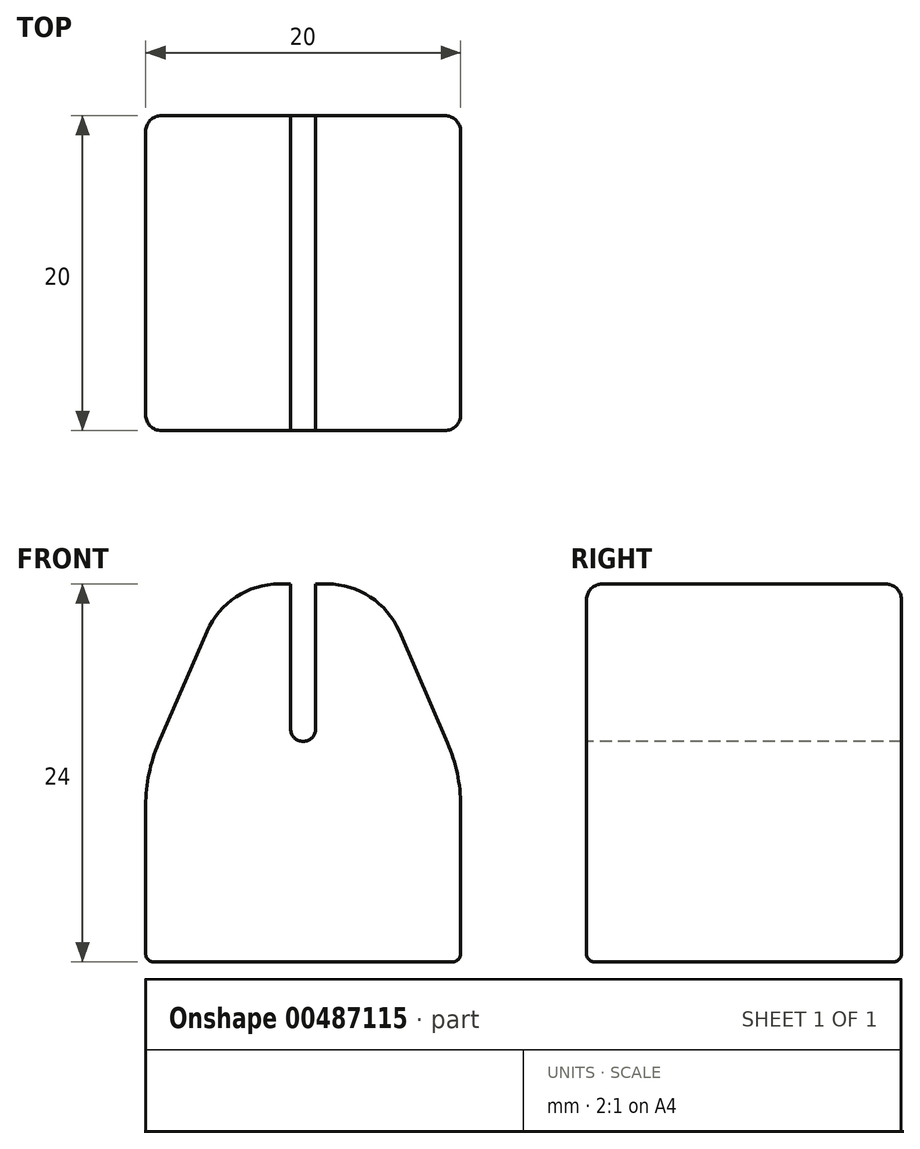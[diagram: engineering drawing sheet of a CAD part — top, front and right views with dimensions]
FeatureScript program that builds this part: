
annotation { "Feature Type Name" : "Feature", "Feature Type Description" : "" }
export const myFeature = defineFeature(function(context is Context, id is Id, definition is map)
    precondition{}
    {
        {
            var Q0;
            Q0=qCreatedBy(makeId("Front.planeOp"),FACE);
            var sketch = newSketch(context, id + "F0", { "sketchPlane" : qUnion([Q0])});
            skLineSegment(sketch, "E0.0.1", {"start": v(-4.8, 10) * mm, "end": v(-10, -2) * mm});
            skLineSegment(sketch, "E0.0.3", {"start": v(-0.8, 0) * mm, "end": v(-0.8, 10) * mm});
            skLineSegment(sketch, "E0.0.4", {"start": v(-0.8, 10) * mm, "end": v(-4.8, 10) * mm});
            skLineSegment(sketch, "E1.0.3", {"start": v(0.8, 10) * mm, "end": v(0.8, 0) * mm});
            skLineSegment(sketch, "E2", {"start": v(-10, -2) * mm, "end": v(-10, -14) * mm});
            skLineSegment(sketch, "E3", {"start": v(-10, -14) * mm, "end": v(10, -14) * mm});
            skLineSegment(sketch, "E4", {"start": v(0.8, 0) * mm, "end": v(-0.8, 0) * mm});
            skLineSegment(sketch, "E5", {"start": v(0, 0) * mm, "end": v(0, -14) * mm});
            skLineSegment(sketch, "E6.MirrorCS", {"start": v(10, -2) * mm, "end": v(10, -14) * mm});
            skLineSegment(sketch, "E7.MirrorCS", {"start": v(4.8, 10) * mm, "end": v(10, -2) * mm});
            skLineSegment(sketch, "E8.MirrorCS", {"start": v(0.8, 10) * mm, "end": v(4.8, 10) * mm});
            skLineSegment(sketch, "E9", {"start": v(-10, -2) * mm, "end": v(10, -2) * mm});
            skLineSegment(sketch, "E10", {"start": v(0, 0) * mm, "end": v(0, -2) * mm});
            skSolve(sketch);
        }
        {
            var Q0;
            Q0=makeQuery(id+"F0.imprint","IMPRINT",FACE,{"disambiguationData":[TD([[makeQuery(id+"F0.imprint","IMPRINT",EDGE,{"derivedFrom":sQuery(id+"F0.wireOp",EDGE,"E0.0.1")}),1.0]])]});
            var Q1;
            Q1=makeQuery(id+"F0.imprint","IMPRINT",FACE,{"disambiguationData":[TD([[makeQuery(id+"F0.imprint","IMPRINT",EDGE,{"derivedFrom":sQuery(id+"F0.wireOp",EDGE,"E1.0.2")}),1.0]])]});
            var Q2;
            {var subQ2=sQuery(id+"F0.wireOp",EDGE,"E1.0.3");Q2=makeQuery(id+"F0.imprint","IMPRINT",FACE,{"disambiguationData":[TD([[makeQuery(id+"F0.imprint","IMPRINT",EDGE,{"derivedFrom":subQ2}),1.0]])]});}
            var Q3;
            {var subQ0=sQuery(id+"F0.wireOp",EDGE,"E2");Q3=makeQuery(id+"F0.imprint","IMPRINT",FACE,{"disambiguationData":[TD([[makeQuery(id+"F0.imprint","IMPRINT",EDGE,{"derivedFrom":subQ0}),1.0]])]});}
            var Q4;
            {var subQ2=sQuery(id+"F0.wireOp",EDGE,"E5");Q4=makeQuery(id+"F0.imprint","IMPRINT",FACE,{"disambiguationData":[TD([[makeQuery(id+"F0.imprint","IMPRINT",EDGE,{"derivedFrom":subQ2}),1.0]])]});}
            extrude(context, id + "F1", {"entities" : qUnion([Q0, Q1, Q2, Q3, Q4]), "endBound" : BoundingType.SYMMETRIC, "depth" : 20 * mm, "offsetDistance" : 25 * mm});
        }
        {
            var Q0;
            Q0=makeQuery(id+"F1.opExtrude","SWEPT_EDGE",EDGE,{"disambiguationData":[OSD([sQuery(id+"F0.wireOp",EDGE,"E6.MirrorCS"),sQuery(id+"F0.wireOp",EDGE,"E7.MirrorCS")])]});
            var Q1;
            Q1=makeQuery(id+"F1.opExtrude","SWEPT_EDGE",EDGE,{"disambiguationData":[OSD([sQuery(id+"F0.wireOp",EDGE,"E0.0.1"),sQuery(id+"F0.wireOp",EDGE,"E2")])]});
            fillet(context, id + "F2", {"entities" : qUnion([Q0, Q1]), "radius" : 10 * mm, "tangentPropagation" : true, "allowEdgeOverflow" : false});
        }
        {
            var Q0;
            Q0=makeQuery(id+"F1.opExtrude","SWEPT_EDGE",EDGE,{"disambiguationData":[OSD([sQuery(id+"F0.wireOp",EDGE,"E7.MirrorCS"),sQuery(id+"F0.wireOp",EDGE,"E8.MirrorCS")])]});
            var Q1;
            Q1=makeQuery(id+"F1.opExtrude","SWEPT_EDGE",EDGE,{"disambiguationData":[OSD([sQuery(id+"F0.wireOp",EDGE,"E0.0.1"),sQuery(id+"F0.wireOp",EDGE,"E0.0.4")])]});
            fillet(context, id + "F3", {"entities" : qUnion([Q0, Q1]), "radius" : 5 * mm, "tangentPropagation" : true, "allowEdgeOverflow" : false});
        }
        {
            var Q0;
            Q0=makeQuery(id+"F1.opExtrude","CAP_EDGE",EDGE,{"disambiguationData":[OSD([sQuery(id+"F0.wireOp",EDGE,"E7.MirrorCS")])],"isStart":true});
            var Q1;
            Q1=makeQuery(id+"F1.opExtrude","CAP_EDGE",EDGE,{"disambiguationData":[OSD([sQuery(id+"F0.wireOp",EDGE,"E7.MirrorCS")])],"isStart":false});
            var Q2;
            Q2=makeQuery(id+"F1.opExtrude","CAP_EDGE",EDGE,{"disambiguationData":[OSD([sQuery(id+"F0.wireOp",EDGE,"E0.0.1")])],"isStart":true});
            var Q3;
            Q3=makeQuery(id+"F1.opExtrude","CAP_EDGE",EDGE,{"disambiguationData":[OSD([sQuery(id+"F0.wireOp",EDGE,"E0.0.1")])],"isStart":false});
            fillet(context, id + "F4", {"entities" : qUnion([Q0, Q1, Q2, Q3]), "radius" : 1 * mm, "tangentPropagation" : true, "allowEdgeOverflow" : false});
        }
        {
            var Q0;
            Q0=makeQuery(id+"F1.opExtrude","SWEPT_EDGE",EDGE,{"disambiguationData":[OSD([sQuery(id+"F0.wireOp",EDGE,"E0.0.3"),sQuery(id+"F0.wireOp",EDGE,"E4")])]});
            var Q1;
            Q1=makeQuery(id+"F1.opExtrude","SWEPT_EDGE",EDGE,{"disambiguationData":[OSD([sQuery(id+"F0.wireOp",EDGE,"E1.0.3"),sQuery(id+"F0.wireOp",EDGE,"E4")])]});
            fillet(context, id + "F5", {"entities" : qUnion([Q0, Q1]), "radius" : .8 * mm, "tangentPropagation" : true, "allowEdgeOverflow" : false});
        }
        {
            var Q0;
            Q0=makeQuery(id+"F1.opExtrude","SWEPT_FACE",FACE,{"disambiguationData":[OSD([sQuery(id+"F0.wireOp",EDGE,"E3")])]});
            fillet(context, id + "F6", {"entities" : qUnion([Q0]), "radius" : .5 * mm, "tangentPropagation" : true, "allowEdgeOverflow" : false});
        }
    });
